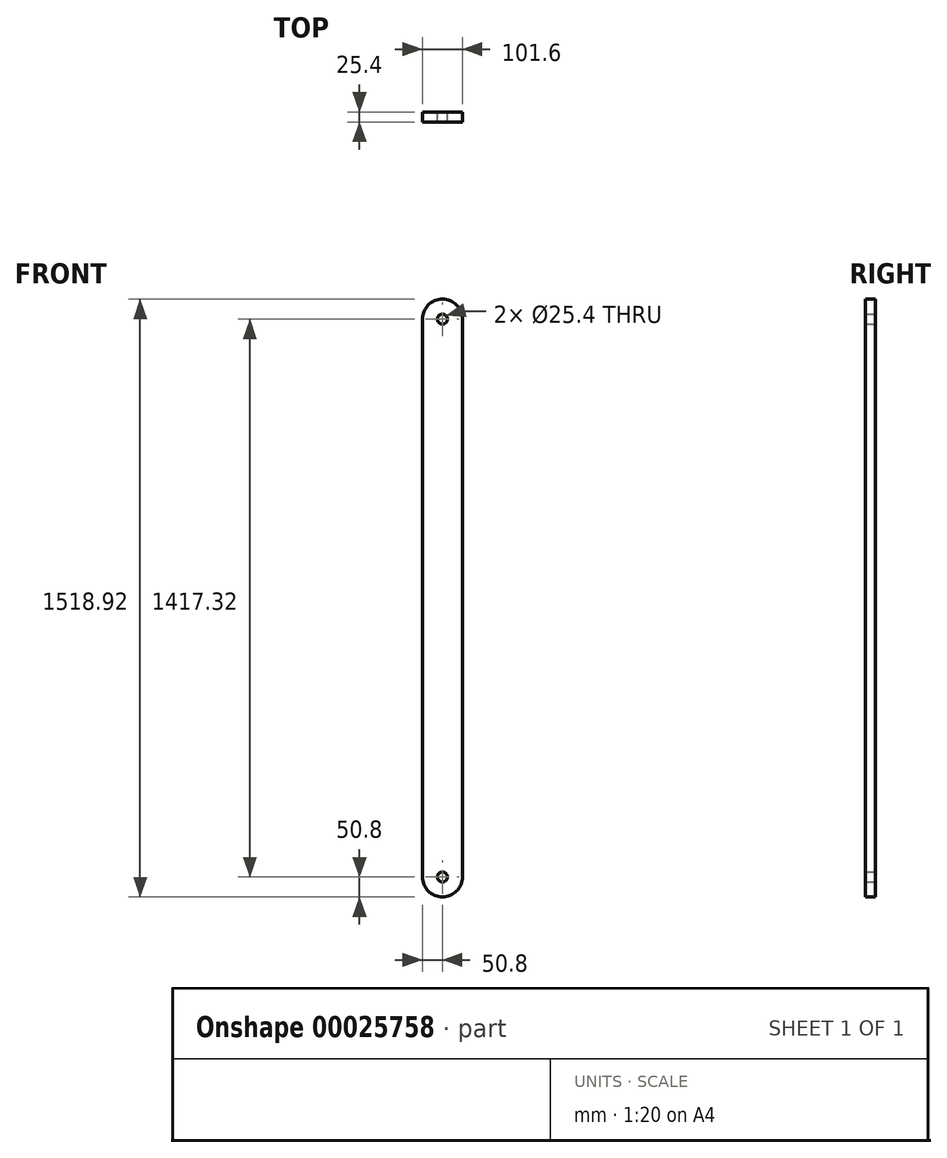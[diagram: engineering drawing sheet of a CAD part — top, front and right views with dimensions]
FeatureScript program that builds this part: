
annotation { "Feature Type Name" : "Feature", "Feature Type Description" : "" }
export const myFeature = defineFeature(function(context is Context, id is Id, definition is map)
    precondition{}
    {
        {
            var Q0;
            Q0=qCreatedBy(makeId("Front.planeOp"),FACE);
            var sketch = newSketch(context, id + "F0", { "sketchPlane" : qUnion([Q0])});
            skCircle(sketch, "E0", {"center": v(0, 0) * mm, "radius": 12.7 * mm});
            skLineSegment(sketch, "E1", {"start": v(-50.8, 0) * mm, "end": v(-50.8, 1417.32) * mm});
            skLineSegment(sketch, "E2", {"start": v(50.8, 0) * mm, "end": v(50.8, 1417.32) * mm});
            skArc(sketch, "E3", {"start": v(-50.8, 0) * mm, "mid": v(0, -50.8) * mm, "end": v(50.8, 0) * mm});
            skArc(sketch, "E4", {"start": v(50.8, 1417.32) * mm, "mid": v(0, 1468.12) * mm, "end": v(-50.8, 1417.32) * mm});
            skCircle(sketch, "E5", {"center": v(0, 1417.32) * mm, "radius": 12.7 * mm});
            skSolve(sketch);
        }
        {
            var Q0;
            Q0 = qSketchRegion(id + "F0", true);
            extrude(context, id + "F1", {"entities" : qUnion([Q0]), "depth" : 25.4 * mm});
        }
    });
